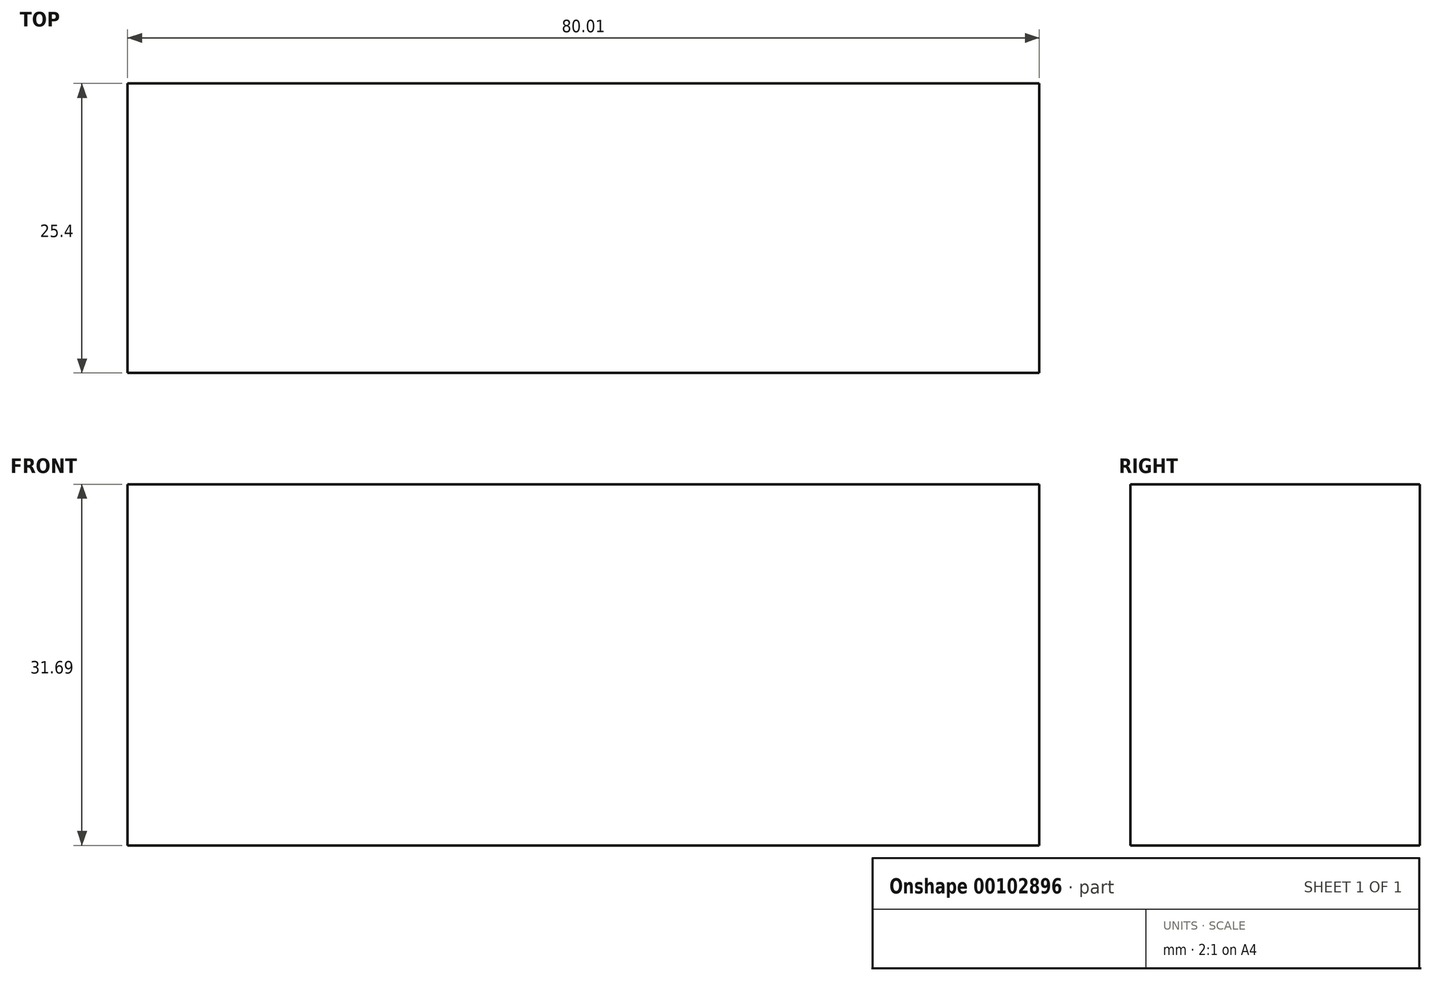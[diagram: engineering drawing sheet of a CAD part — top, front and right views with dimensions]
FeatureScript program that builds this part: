
annotation { "Feature Type Name" : "Feature", "Feature Type Description" : "" }
export const myFeature = defineFeature(function(context is Context, id is Id, definition is map)
    precondition{}
    {
        {
            var Q0;
            Q0=qCreatedBy(makeId("Front.planeOp"),FACE);
            var sketch = newSketch(context, id + "F0", { "sketchPlane" : qUnion([Q0])});
            skLineSegment(sketch, "E0.bottom", {"start": v(-49.42, 40.79) * mm, "end": v(30.6, 40.79) * mm});
            skLineSegment(sketch, "E0.top", {"start": v(-49.42, 9.1) * mm, "end": v(30.6, 9.1) * mm});
            skLineSegment(sketch, "E0.left", {"start": v(-49.42, 40.79) * mm, "end": v(-49.42, 9.1) * mm});
            skLineSegment(sketch, "E0.right", {"start": v(30.6, 40.79) * mm, "end": v(30.6, 9.1) * mm});
            skSolve(sketch);
        }
        {
            var Q0;
            Q0 = qSketchRegion(id + "F0", true);
            extrude(context, id + "F1", {"entities" : qUnion([Q0]), "depth" : 25.4 * mm});
        }
    });
